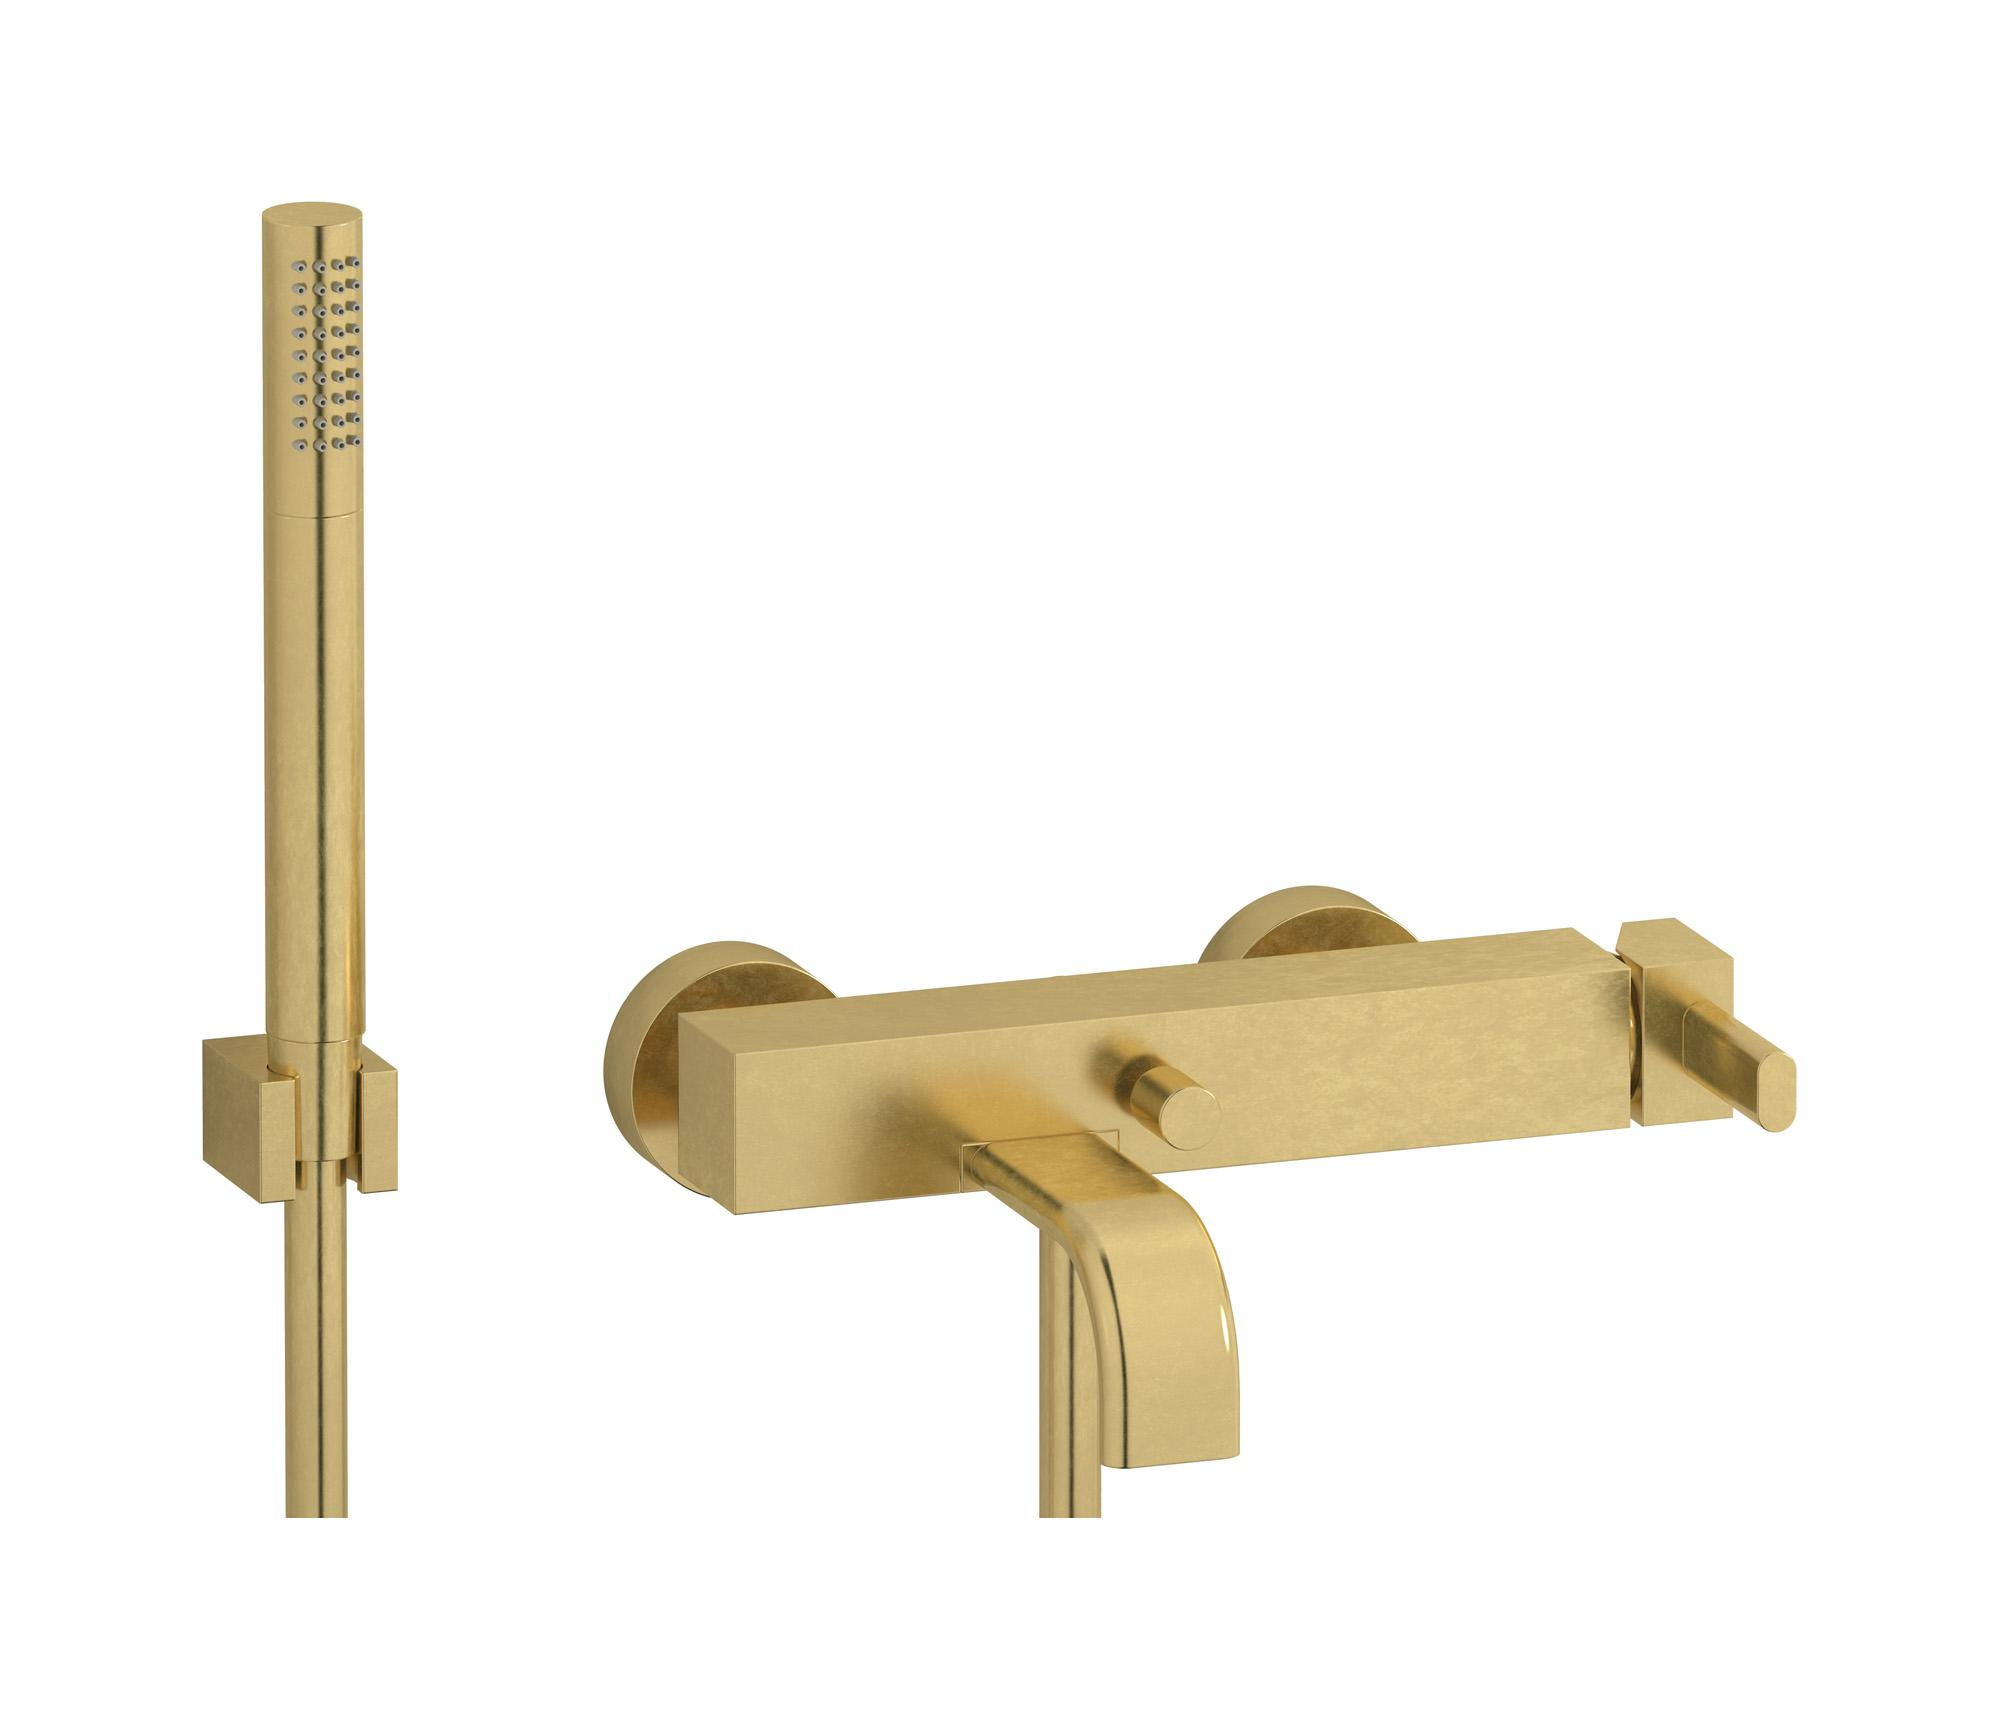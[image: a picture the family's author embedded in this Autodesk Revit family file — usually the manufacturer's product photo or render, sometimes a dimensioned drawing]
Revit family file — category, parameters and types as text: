
# Revit family: SB250
name_source: partatom
category: Apparecchi idraulici
units: mm (PartAtom-declared; Revit-internal decimal feet)

## family parameters
Basato su piano di lavoro = No
Condiviso = No
Mantieni orientamento annotazione = No
Numero OmniClass = 23.45.55.17
Punto di calcolo locali = No
Quota connettore circolare = Usa diametro
Sempre verticale = Sì
Taglio con vuoti quando caricato = No
Tipo di parte = Normale
Titolo OmniClass = Mixing Faucets

## types (6) — shared parameters
Cold water inlet = 10 mm  [stored 0.0328084 ft]
Commenti sul tipo = Bath filler
Connessione CW = No
Connessione HW = No
Connessione di scarico = No
Connessione di ventilazione = No
Descrizione = Wall mounted bath filler complete with shower kit
Hot water inlet = 10 mm  [stored 0.0328084 ft]
Produttore = IB Rubinetterie S.p.A.
URL = https://www.weareib.it
zero-valued in all types: Prospetto di default

## per-type parameters (varying)
| type | Finishes surface | Immagine tipo | Modello |
| Chrome | IB_Chrome | SB250CC.jpg | SB250CC |
| Brushed nickel | IB_Brushed nickel | SB250SS.jpg | SB250SS |
| Matt black | IB_matt black | SB250NP.jpg | SB250NP |
| Natural brass | IB_Brass | SB250ON.jpg | SB250ON |
| Brushed gold | IB_brushed gold | SB250OS.jpg | SB250OS |
| Rose gold | IB_Rose gold | SB250RS.jpg | SB250RS |

note: [stored X ft] marks values corroborated as IEEE doubles in the binary element streams (Revit-internal decimal feet)
